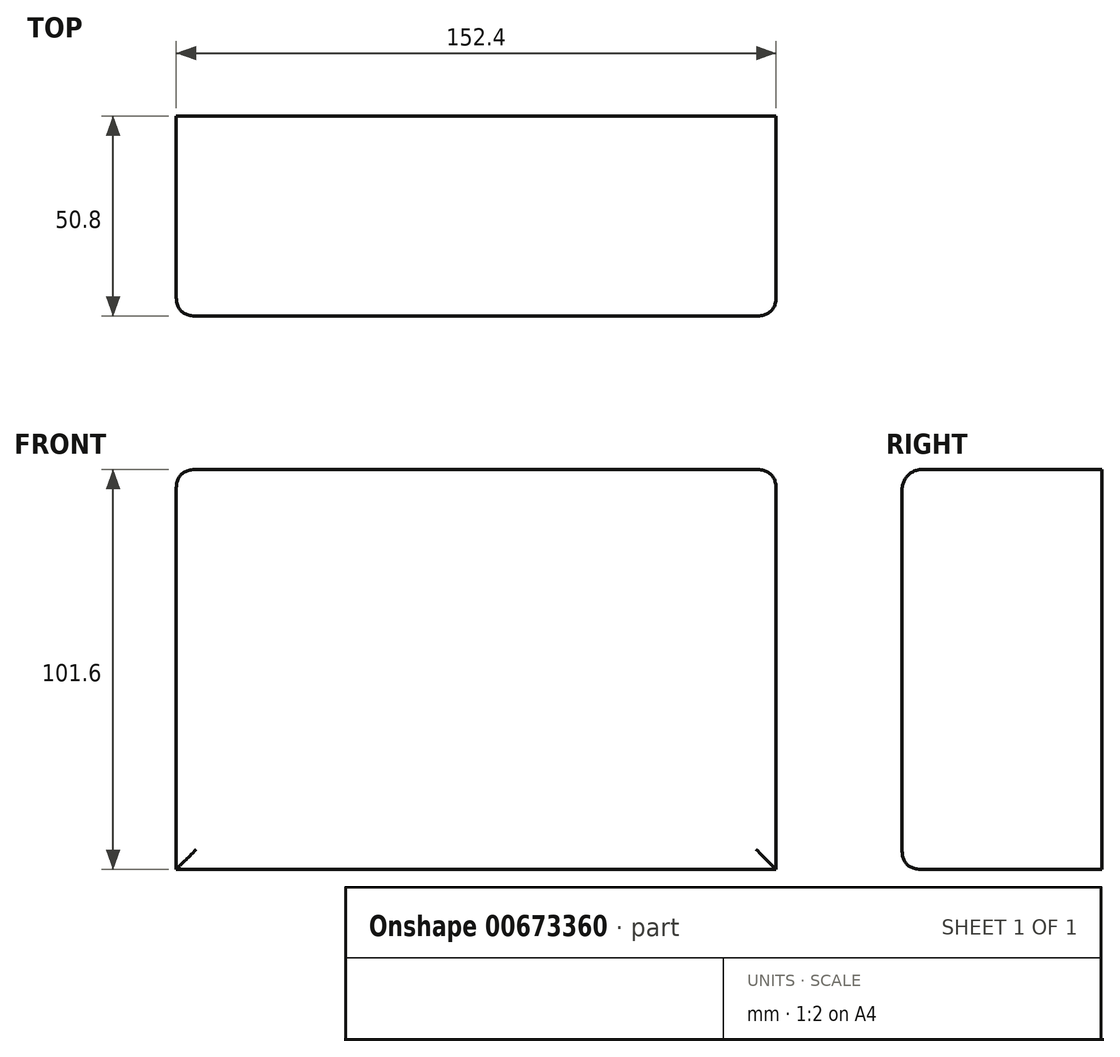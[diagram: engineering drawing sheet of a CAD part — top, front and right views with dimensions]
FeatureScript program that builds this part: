
annotation { "Feature Type Name" : "Feature", "Feature Type Description" : "" }
export const myFeature = defineFeature(function(context is Context, id is Id, definition is map)
    precondition{}
    {
        {
            var Q0;
            Q0=qCreatedBy(makeId("Front.planeOp"),FACE);
            var sketch = newSketch(context, id + "F0", { "sketchPlane" : qUnion([Q0])});
            skLineSegment(sketch, "E0.bottom", {"start": v(-152.4, 73.51) * mm, "end": v(0, 73.51) * mm});
            skLineSegment(sketch, "E0.top", {"start": v(-152.4, -28.09) * mm, "end": v(0, -28.09) * mm});
            skLineSegment(sketch, "E0.left", {"start": v(-152.4, 73.51) * mm, "end": v(-152.4, -28.09) * mm});
            skLineSegment(sketch, "E0.right", {"start": v(0, 73.51) * mm, "end": v(0, -28.09) * mm});
            skSolve(sketch);
        }
        {
            var Q0;
            Q0=makeQuery(id+"F0.imprint","IMPRINT",FACE,{"disambiguationData":[TD([[makeQuery(id+"F0.imprint","IMPRINT",EDGE,{"derivedFrom":sQuery(id+"F0.wireOp",EDGE,"E0.bottom")}),-1.0]])]});
            extrude(context, id + "F1", {"entities" : qUnion([Q0]), "depth" : 50.8 * mm, "offsetDistance" : 25.4 * mm});
        }
        {
            var Q0;
            Q0=makeQuery(id+"F1.opExtrude","CAP_EDGE",EDGE,{"disambiguationData":[OSD([sQuery(id+"F0.wireOp",EDGE,"E0.bottom")])],"isStart":false});
            fillet(context, id + "F2", {"entities" : qUnion([Q0]), "radius" : 5.08 * mm, "tangentPropagation" : true, "allowEdgeOverflow" : false});
        }
        {
            var Q0;
            Q0=makeQuery(id+"F1.opExtrude","CAP_FACE",FACE,{"disambiguationData":[OSD([sQuery(id+"F0.wireOp",EDGE,"E0.bottom"),sQuery(id+"F0.wireOp",EDGE,"E0.top"),sQuery(id+"F0.wireOp",EDGE,"E0.left"),sQuery(id+"F0.wireOp",EDGE,"E0.right")])],"isStart":false});
            fillet(context, id + "F3", {"entities" : qUnion([Q0]), "tangentPropagation" : true, "crossSection" : FilletCrossSection.CONIC, "radius" : 5.08 * mm, "rho" : 0.5, "defaultsChanged" : false, "vertexSettings" : [], "allowEdgeOverflow" : false});
        }
    });
